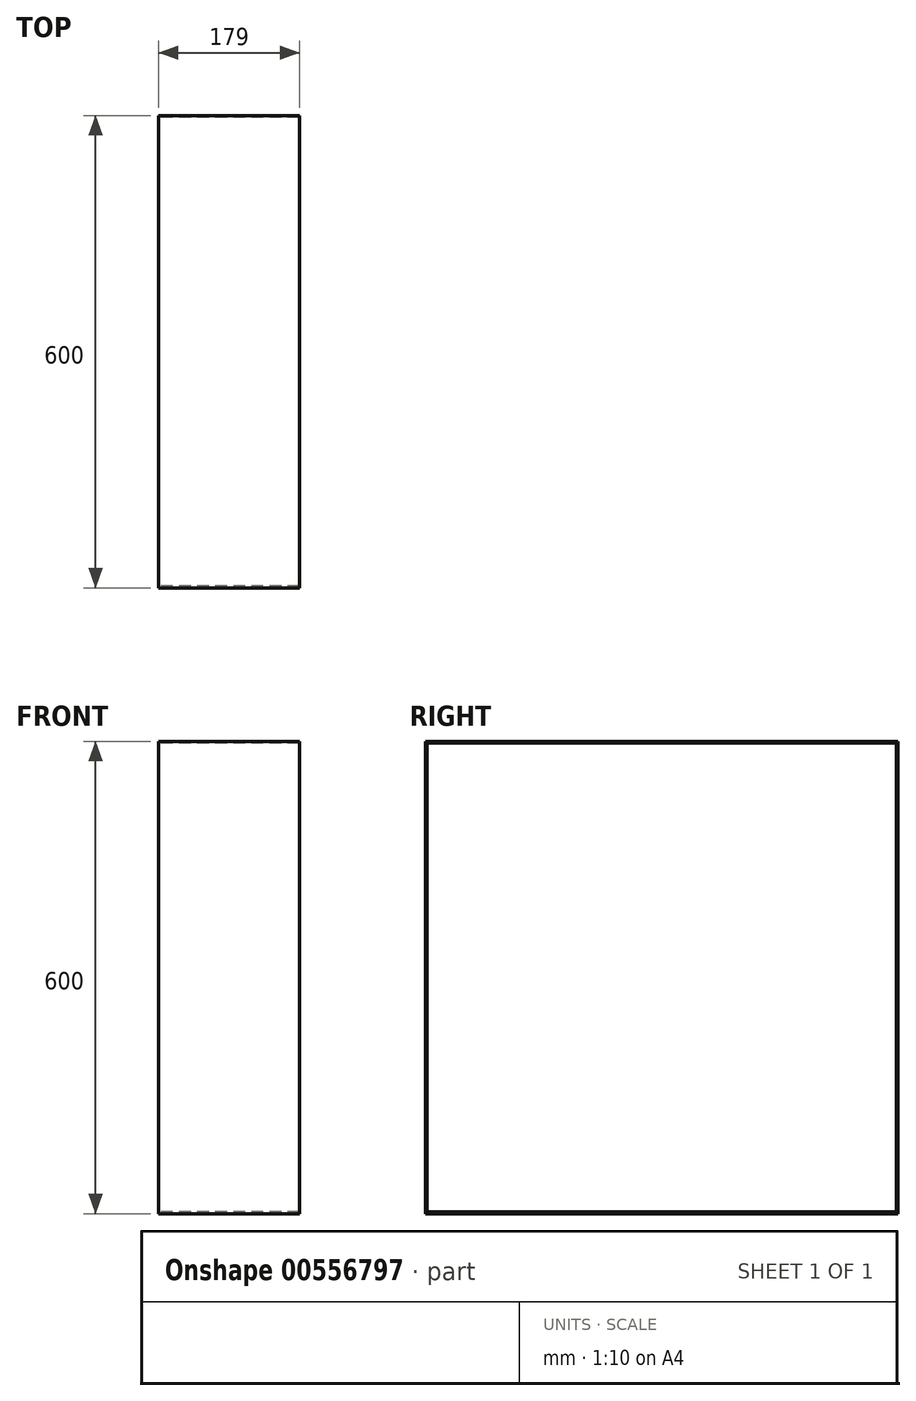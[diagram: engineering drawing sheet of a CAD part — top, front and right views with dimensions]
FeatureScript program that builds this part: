
annotation { "Feature Type Name" : "Feature", "Feature Type Description" : "" }
export const myFeature = defineFeature(function(context is Context, id is Id, definition is map)
    precondition{}
    {
        {
            var Q0;
            Q0=qCreatedBy(makeId("Right.planeOp"),FACE);
            var sketch = newSketch(context, id + "F0", { "sketchPlane" : qUnion([Q0])});
            skLineSegment(sketch, "E0", {"start": v(-190.86, -297.99) * mm, "end": v(405.14, -297.99) * mm});
            skLineSegment(sketch, "E1", {"start": v(-192.86, -299.99) * mm, "end": v(407.14, -299.99) * mm});
            skLineSegment(sketch, "E2", {"start": v(405.14, 298.01) * mm, "end": v(-190.86, 298.01) * mm});
            skLineSegment(sketch, "E3", {"start": v(407.14, 300.01) * mm, "end": v(-192.86, 300.01) * mm});
            skLineSegment(sketch, "E4", {"start": v(-192.86, 300.01) * mm, "end": v(-192.86, -299.99) * mm});
            skLineSegment(sketch, "E5", {"start": v(-190.86, 298.01) * mm, "end": v(-190.86, -297.99) * mm});
            skLineSegment(sketch, "E6", {"start": v(-139.36, -3.52) * mm, "end": v(-139.36, 3.48) * mm});
            skLineSegment(sketch, "E7", {"start": v(-146.36, 3.48) * mm, "end": v(-146.36, -3.52) * mm});
            skLineSegment(sketch, "E8", {"start": v(-139.36, 3.48) * mm, "end": v(-146.36, 3.48) * mm});
            skLineSegment(sketch, "E9", {"start": v(-146.36, -3.52) * mm, "end": v(-139.36, -3.52) * mm});
            skCircle(sketch, "E10", {"center": v(-142.86, -0.02) * mm, "radius": 16.5 * mm});
            skCircle(sketch, "E11", {"center": v(-142.86, -0.02) * mm, "radius": 8.5 * mm});
            skLineSegment(sketch, "E12", {"start": v(405.14, -297.99) * mm, "end": v(405.14, 298.01) * mm});
            skLineSegment(sketch, "E13", {"start": v(407.14, -299.99) * mm, "end": v(407.14, 300.01) * mm});
            skSolve(sketch);
        }
        {
            var Q0;
            Q0=qSketchRegion(id+"F0",true);
            extrude(context, id + "F1", {"entities" : qUnion([Q0]), "depth" : 179 * mm, "offsetDistance" : 25 * mm});
        }
    });
